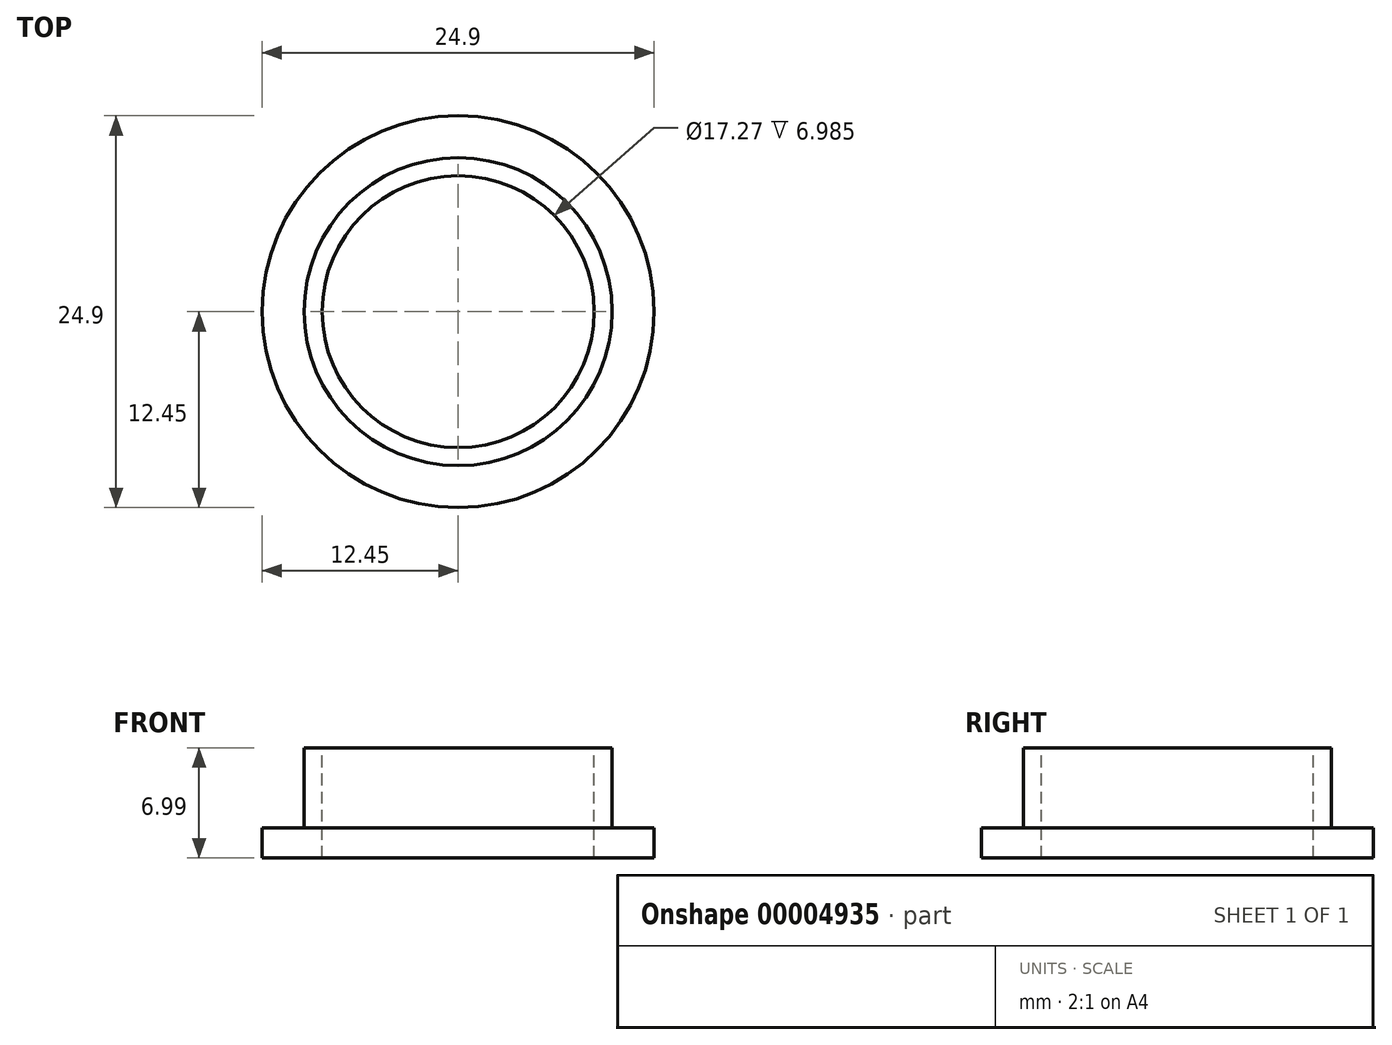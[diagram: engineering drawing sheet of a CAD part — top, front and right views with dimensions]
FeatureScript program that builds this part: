
annotation { "Feature Type Name" : "Feature", "Feature Type Description" : "" }
export const myFeature = defineFeature(function(context is Context, id is Id, definition is map)
    precondition{}
    {
        {
            var Q0;
            Q0=qCreatedBy(makeId("Top.planeOp"),FACE);
            var sketch = newSketch(context, id + "F0", { "sketchPlane" : qUnion([Q0])});
            skCircle(sketch, "E0", {"center": v(0, 0) * mm, "radius": 12.45 * mm});
            skSolve(sketch);
        }
        {
            var Q0;
            Q0=makeQuery(id+"F0.imprint","IMPRINT",FACE,{"disambiguationData":[TD([[makeQuery(id+"F0.imprint","IMPRINT",EDGE,{"derivedFrom":sQuery(id+"F0.wireOp",EDGE,"E0")}),1.0]])]});
            extrude(context, id + "F1", {"entities" : qUnion([Q0]), "depth" : 1.9 * mm});
        }
        {
            var Q0;
            Q0=makeQuery(id+"F1.opExtrude","CAP_FACE",FACE,{"disambiguationData":[OSD([sQuery(id+"F0.wireOp",EDGE,"E0")])],"isStart":false});
            var sketch = newSketch(context, id + "F2", { "sketchPlane" : qUnion([Q0])});
            skCircle(sketch, "E1", {"center": v(0, 0) * mm, "radius": 9.78 * mm});
            skSolve(sketch);
        }
        {
            var Q0;
            Q0=makeQuery(id+"F2.imprint","IMPRINT",FACE,{"disambiguationData":[TD([[makeQuery(id+"F2.imprint","IMPRINT",EDGE,{"derivedFrom":sQuery(id+"F2.wireOp",EDGE,"E1")}),1.0]])]});
            extrude(context, id + "F3", {"entities" : qUnion([Q0]), "operationType" : NewBodyOperationType.ADD, "depth" : 5.08 * mm});
        }
        {
            var Q0;
            Q0=makeQuery(id+"F3.opExtrude","CAP_FACE",FACE,{"disambiguationData":[OSD([sQuery(id+"F2.wireOp",EDGE,"E1")])],"isStart":false});
            var sketch = newSketch(context, id + "F4", { "sketchPlane" : qUnion([Q0])});
            skCircle(sketch, "E2", {"center": v(0, 0) * mm, "radius": 8.64 * mm});
            skSolve(sketch);
        }
        {
            var Q0;
            Q0 = qSketchRegion(id + "F4", true);
            extrude(context, id + "F5", {"entities" : qUnion([Q0]), "operationType" : NewBodyOperationType.REMOVE, "endBound" : BoundingType.THROUGH_ALL, "oppositeDirection" : true, "depth" : 25.4 * mm});
        }
    });
